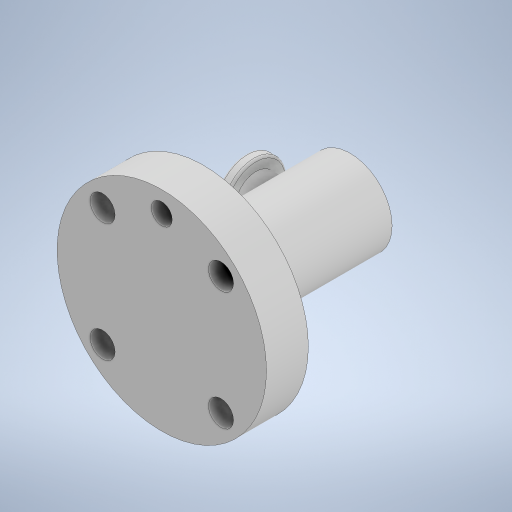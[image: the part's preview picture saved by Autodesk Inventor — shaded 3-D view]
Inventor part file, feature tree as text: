
AUTODESK INVENTOR PART (.ipt)
format: ipt  version: 2024 (Build 280153000, 153)  size: 316,416 bytes
history: native  units: mm
features: extrude x7, sketch x7, fillet x3, plane x2, thread x1
ambient origin geometry x8: Origin, YZ Plane, XZ Plane, XY Plane, X Axis, Y Axis, Z Axis, Center Point
bodies: Body1 (feature_tree)
feature tree (20):
  extrude  "Extrusión3"  Depth=15.164mm
  extrude  "Extrusión4"  Depth=25.0mm TaperAngle=0.0deg
  plane  "Plano de trabajo2"
  extrude  "Extrusión5"  Depth=10.0mm
  plane  "Plano de trabajo3"
  extrude  "Extrusión6"  [1 undecoded]
  fillet  "Empalme1"  Radius=0.5mm
  extrude  "Extrusión7"  Depth=0.5mm
  fillet  "Empalme2"  Radius=0.5mm
  fillet  "Empalme3"  Radius=2.5mm
  extrude  "Extrusión8"  Depth=10.0mm
  extrude  "Extrusión9"  Depth=10.0mm TaperAngle=0.0deg
  thread  "Rosca1"  [1 undecoded]
  sketch  "Boceto4"  dims[d6=20.0mm d7=15.164mm]
  sketch  "Boceto5"  dims[d8=40.0mm d9=0.0mm d10=25.0mm d11=0.0mm]
  sketch  "Boceto6"  dims[d14=10.0mm d15=10.0mm]
  sketch  "Boceto8"  dims[d16=10.0mm d17=0.0mm d20=-5.0mm]
  sketch  "Boceto9"  dims[d21=15.0mm d22=5.0mm d23=2.5mm d24=0.0mm d25=0.5mm]
  sketch  "Boceto10"  dims[d26=1.5mm d27=0.0mm d28=0.5mm d29=0.5mm d30=2.5mm d31=0.0mm]
  sketch  "Boceto11"  dims[d32=5.0mm d33=0.0mm d34=50.0mm d35=10.0mm d36=0.0mm d37=45.0deg d38=45.0deg d39=20.0mm d40=6.0mm d41=6.0mm d42=20.0mm d43=5.0mm d44=15.0mm d45=0.0mm]
note: 2 required parameter values undecoded (feature->parameter linkage not recoverable at this tier; creation-order binding heuristic only, values carry confidence <= 0.55)
